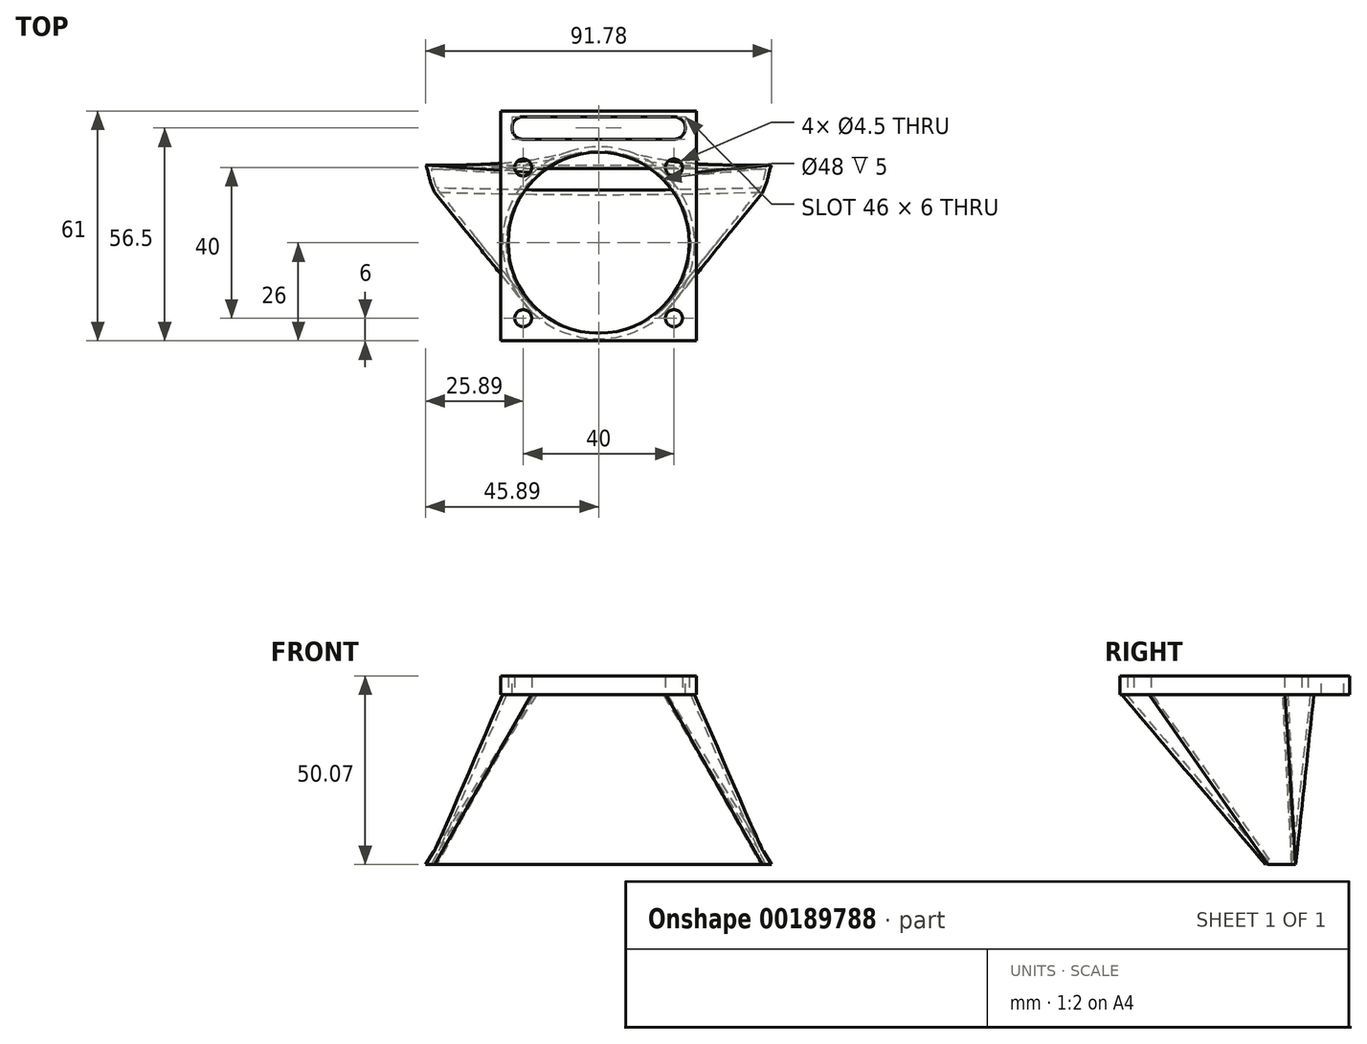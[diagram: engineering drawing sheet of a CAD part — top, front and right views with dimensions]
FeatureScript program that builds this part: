
annotation { "Feature Type Name" : "Feature", "Feature Type Description" : "" }
export const myFeature = defineFeature(function(context is Context, id is Id, definition is map)
    precondition{}
    {
        {
            var Q0;
            Q0=qCreatedBy(makeId("Top.planeOp"),FACE);
            var sketch = newSketch(context, id + "F0", { "sketchPlane" : qUnion([Q0])});
            skLineSegment(sketch, "E0.bottom", {"start": v(26, -26) * mm, "end": v(-26, -26) * mm});
            skLineSegment(sketch, "E0.top", {"start": v(26, 26) * mm, "end": v(-26, 26) * mm});
            skLineSegment(sketch, "E0.left", {"start": v(26, -26) * mm, "end": v(26, 26) * mm});
            skLineSegment(sketch, "E0.right", {"start": v(-26, -26) * mm, "end": v(-26, 26) * mm});
            skPoint(sketch, "E0.middle", {"position": v(0, 0) * mm});
            skLineSegment(sketch, "E1.bottom", {"start": v(20, -20) * mm, "end": v(-20, -20) * mm, "construction": true});
            skLineSegment(sketch, "E1.top", {"start": v(20, 20) * mm, "end": v(-20, 20) * mm, "construction": true});
            skLineSegment(sketch, "E1.left", {"start": v(20, -20) * mm, "end": v(20, 20) * mm, "construction": true});
            skLineSegment(sketch, "E1.right", {"start": v(-20, -20) * mm, "end": v(-20, 20) * mm, "construction": true});
            skCircle(sketch, "E2", {"center": v(-20, 20) * mm, "radius": 2.25 * mm});
            skCircle(sketch, "E3", {"center": v(20, 20) * mm, "radius": 2.25 * mm});
            skCircle(sketch, "E4", {"center": v(-20, -20) * mm, "radius": 2.25 * mm});
            skCircle(sketch, "E5", {"center": v(20, -20) * mm, "radius": 2.25 * mm});
            skCircle(sketch, "E6", {"center": v(0, 0) * mm, "radius": 24 * mm});
            skSolve(sketch);
        }
        {
            var Q0;
            Q0 = qSketchRegion(id + "F0", true);
            extrude(context, id + "F1", {"entities" : qUnion([Q0]), "depth" : 5 * mm});
        }
        {
            var Q0;
            Q0=makeQuery(id+"F1.opExtrude","CAP_FACE",FACE,{"disambiguationData":[OSD([sQuery(id+"F0.wireOp",EDGE,"E0.bottom"),sQuery(id+"F0.wireOp",EDGE,"E0.top"),sQuery(id+"F0.wireOp",EDGE,"E0.left"),sQuery(id+"F0.wireOp",EDGE,"E0.right"),sQuery(id+"F0.wireOp",EDGE,"E2"),sQuery(id+"F0.wireOp",EDGE,"E3"),sQuery(id+"F0.wireOp",EDGE,"E4"),sQuery(id+"F0.wireOp",EDGE,"E5"),sQuery(id+"F0.wireOp",EDGE,"E6")])],"isStart":false});
            var sketch = newSketch(context, id + "F2", { "sketchPlane" : qUnion([Q0])});
            skLineSegment(sketch, "E7.bottom", {"start": v(-26, 26) * mm, "end": v(26, 26) * mm});
            skLineSegment(sketch, "E7.top", {"start": v(-26, 35) * mm, "end": v(26, 35) * mm});
            skLineSegment(sketch, "E7.left", {"start": v(-26, 26) * mm, "end": v(-26, 35) * mm});
            skLineSegment(sketch, "E7.right", {"start": v(26, 26) * mm, "end": v(26, 35) * mm});
            skLineSegment(sketch, "E8", {"start": v(-26, 30.5) * mm, "end": v(26, 30.5) * mm, "construction": true});
            skArc(sketch, "E9", {"start": v(-20, 33.5) * mm, "mid": v(-23, 30.5) * mm, "end": v(-20, 27.5) * mm});
            skArc(sketch, "E10", {"start": v(20, 27.5) * mm, "mid": v(23, 30.5) * mm, "end": v(20, 33.5) * mm});
            skLineSegment(sketch, "E11", {"start": v(-20, 33.5) * mm, "end": v(20, 33.5) * mm});
            skLineSegment(sketch, "E12", {"start": v(-20, 27.5) * mm, "end": v(20, 27.5) * mm});
            skSolve(sketch);
        }
        {
            var Q0;
            Q0 = qSketchRegion(id + "F2", true);
            extrude(context, id + "F3", {"entities" : qUnion([Q0]), "operationType" : NewBodyOperationType.ADD, "oppositeDirection" : true, "depth" : 5 * mm});
        }
        {
            var Q0;
            Q0=makeQuery(id+"F3.boolean.opBoolean","MERGE",FACE,{"derivedFrom":[makeQuery(id+"F1.opExtrude","SWEPT_FACE",FACE,{"disambiguationData":[OSD([sQuery(id+"F0.wireOp",EDGE,"E0.right")])]}),makeQuery(id+"F3.opExtrude","SWEPT_FACE",FACE,{"disambiguationData":[OSD([sQuery(id+"F2.wireOp",EDGE,"E7.left")])]})]});
            var sketch = newSketch(context, id + "F4", { "sketchPlane" : qUnion([Q0])});
            skLineSegment(sketch, "E13", {"start": v(26, 0) * mm, "end": v(-19.96, -45.96) * mm, "construction": true});
            skLineSegment(sketch, "E14", {"start": v(-19.96, -45.96) * mm, "end": v(-50.46, -15.46) * mm, "construction": true});
            skLineSegment(sketch, "E15", {"start": v(-35, 0) * mm, "end": v(-50.46, -15.46) * mm, "construction": true});
            skSolve(sketch);
        }
        {
            var Q0;
            Q0=sQuery(id+"F4.wireOp",EDGE,"E14");
            cPlane(context, id + "F5", {"entities" : qUnion([Q0]), "cplaneType" : CPlaneType.LINE_ANGLE, "offset" : 25 * mm, "angle" : 0 * degree, "width" : 150 * mm, "height" : 150 * mm});
        }
        {
            var Q0;
            Q0=qCreatedBy(id+"F5.planeOp",FACE);
            var sketch = newSketch(context, id + "F6", { "sketchPlane" : qUnion([Q0])});
            skLineSegment(sketch, "E16.bottom", {"start": v(26, -18.38) * mm, "end": v(-26, -18.38) * mm, "construction": true});
            skLineSegment(sketch, "E17.bottom", {"start": v(46, -17.38) * mm, "end": v(-46, -17.38) * mm});
            skLineSegment(sketch, "E17.top", {"start": v(46, -23.38) * mm, "end": v(-46, -23.38) * mm});
            skLineSegment(sketch, "E17.left", {"start": v(46, -17.38) * mm, "end": v(46, -23.38) * mm});
            skLineSegment(sketch, "E17.right", {"start": v(-46, -17.38) * mm, "end": v(-46, -23.38) * mm});
            skSolve(sketch);
        }
        {
            var Q0;
            Q0=makeQuery(id+"F3.boolean.opBoolean","MERGE",FACE,{"derivedFrom":[makeQuery(id+"F1.opExtrude","CAP_FACE",FACE,{"disambiguationData":[OSD([sQuery(id+"F0.wireOp",EDGE,"E0.bottom"),sQuery(id+"F0.wireOp",EDGE,"E0.top"),sQuery(id+"F0.wireOp",EDGE,"E0.left"),sQuery(id+"F0.wireOp",EDGE,"E0.right"),sQuery(id+"F0.wireOp",EDGE,"E2"),sQuery(id+"F0.wireOp",EDGE,"E3"),sQuery(id+"F0.wireOp",EDGE,"E4"),sQuery(id+"F0.wireOp",EDGE,"E5"),sQuery(id+"F0.wireOp",EDGE,"E6")])],"isStart":true}),makeQuery(id+"F3.opExtrude","CAP_FACE",FACE,{"disambiguationData":[OSD([sQuery(id+"F2.wireOp",EDGE,"E7.bottom"),sQuery(id+"F2.wireOp",EDGE,"E7.top"),sQuery(id+"F2.wireOp",EDGE,"E7.left"),sQuery(id+"F2.wireOp",EDGE,"E7.right"),sQuery(id+"F2.wireOp",EDGE,"E9"),sQuery(id+"F2.wireOp",EDGE,"E10"),sQuery(id+"F2.wireOp",EDGE,"E11"),sQuery(id+"F2.wireOp",EDGE,"E12")])],"isStart":false})]});
            var sketch = newSketch(context, id + "F7", { "sketchPlane" : qUnion([Q0])});
            skCircle(sketch, "E18", {"center": v(0, 0) * mm, "radius": 24 * mm, "construction": true});
            skArc(sketch, "E19", {"start": v(-17.4, -18.63) * mm, "mid": v(0.52, -25.5) * mm, "end": v(18.16, -17.9) * mm});
            skArc(sketch, "E20", {"start": v(18.16, -17.9) * mm, "mid": v(25.5, 0.24) * mm, "end": v(17.82, 18.24) * mm});
            skArc(sketch, "E21", {"start": v(17.82, 18.24) * mm, "mid": v(-0.04, 25.5) * mm, "end": v(-17.88, 18.18) * mm});
            skArc(sketch, "E22", {"start": v(-17.88, 18.18) * mm, "mid": v(-25.5, -0.33) * mm, "end": v(-17.4, -18.63) * mm});
            skSolve(sketch);
        }
        {
            var Q1;
            Q1 = qSketchRegion(id + "F7", true);
            var Q2;
            Q2 = qSketchRegion(id + "F6", true);
            loft(context, id + "F8", {"sheetProfilesArray" : [{ "sheetProfileEntities" : qUnion([Q1]) }, { "sheetProfileEntities" : qUnion([Q2]) }]});
        }
        {
            var Q0;
            Q0=makeQuery(id+"F8.opLoft","CAP_FACE",FACE,{"disambiguationData":[OSD([makeQuery(id+"F7.imprint","IMPRINT",FACE,{"disambiguationData":[TD([[makeQuery(id+"F7.imprint","IMPRINT",EDGE,{"derivedFrom":sQuery(id+"F7.wireOp",EDGE,"E19")}),1.0]])]})])],"isStart":true});
            var Q1;
            Q1=makeQuery(id+"F8.opLoft","CAP_FACE",FACE,{"disambiguationData":[OSD([makeQuery(id+"F6.imprint","IMPRINT",FACE,{"disambiguationData":[TD([[makeQuery(id+"F6.imprint","IMPRINT",EDGE,{"derivedFrom":sQuery(id+"F6.wireOp",EDGE,"E17.bottom")}),1.0]])]})])],"isStart":true});
            shell(context, id + "F9", {"entities" : qUnion([Q0, Q1]), "thickness" : 1 * mm});
        }
        {
            var Q0;
            Q0=qCreatedBy(makeId("Right.planeOp"),FACE);
            var sketch = newSketch(context, id + "F10", { "sketchPlane" : qUnion([Q0])});
            skLineSegment(sketch, "E23", {"start": v(23.18, -45.07) * mm, "end": v(6.28, -45.07) * mm});
            skLineSegment(sketch, "E24", {"start": v(6.28, -45.07) * mm, "end": v(17.22, -54.06) * mm});
            skLineSegment(sketch, "E25", {"start": v(17.22, -54.06) * mm, "end": v(23.18, -45.07) * mm});
            skSolve(sketch);
        }
        {
            var Q0;
            Q0 = qSketchRegion(id + "F10", true);
            extrude(context, id + "F11", {"entities" : qUnion([Q0]), "operationType" : NewBodyOperationType.REMOVE, "endBound" : BoundingType.SYMMETRIC, "oppositeDirection" : true, "depth" : 200 * mm});
        }
    });
